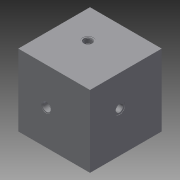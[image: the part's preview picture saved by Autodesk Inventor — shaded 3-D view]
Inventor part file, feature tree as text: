
AUTODESK INVENTOR PART (.ipt)
format: ipt  version: 2014 (Build 180170000, 170)  size: 241,152 bytes
history: native  units: mm
features: other x48, sketch x4, extrude x1
ambient origin geometry x8: Origin, YZ Plane, XZ Plane, XY Plane, X Axis, Y Axis, Z Axis, Center Point
bodies: 实体1 (feature_tree)
feature tree (53):
  extrude  "拉伸1"  TaperAngle=0.0deg  [1 undecoded]
  other  "UCS1"
  other  "UCS2"
  other  "UCS3"
  other  "UCS4"
  other  "UCS5"
  other  "UCS6"
  sketch  "草图1"  dims[d0=200.0mm d1=0.0mm]
  other  "UCS1: YZ 平面"
  other  "UCS1: XZ 平面"
  other  "UCS1: XY 平面"
  other  "UCS1: X 轴"
  other  "UCS1: Y 轴"
  other  "UCS1: Z 轴"
  other  "UCS1: 原点"
  other  "UCS2: YZ 平面"
  other  "UCS2: XZ 平面"
  other  "UCS2: XY 平面"
  other  "UCS2: X 轴"
  other  "UCS2: Y 轴"
  other  "UCS2: Z 轴"
  other  "UCS2: 原点"
  other  "UCS3: YZ 平面"
  other  "UCS3: XZ 平面"
  other  "UCS3: XY 平面"
  other  "UCS3: X 轴"
  other  "UCS3: Y 轴"
  other  "UCS3: Z 轴"
  other  "UCS3: 原点"
  other  "UCS4: YZ 平面"
  other  "UCS4: XZ 平面"
  other  "UCS4: XY 平面"
  other  "UCS4: X 轴"
  other  "UCS4: Y 轴"
  other  "UCS4: Z 轴"
  other  "UCS4: 原点"
  other  "UCS5: YZ 平面"
  other  "UCS5: XZ 平面"
  other  "UCS5: XY 平面"
  other  "UCS5: X 轴"
  other  "UCS5: Y 轴"
  other  "UCS5: Z 轴"
  other  "UCS5: 原点"
  other  "UCS6: YZ 平面"
  other  "UCS6: XZ 平面"
  other  "UCS6: XY 平面"
  other  "UCS6: X 轴"
  other  "UCS6: Y 轴"
  other  "UCS6: Z 轴"
  other  "UCS6: 原点"
  sketch  "草图2"  dims[d2=0.0mm d3=0.0mm d4=0.0mm d5=0.0mm d6=0.0mm d7=0.0mm]
  sketch  "草图3"  dims[d8=0.0mm d9=0.0mm d10=0.0mm d11=0.0mm d12=0.0mm d13=0.0mm]
  sketch  "草图4"  dims[d14=0.0mm d15=0.0mm d16=0.0mm d17=0.0mm d18=0.0mm d19=0.0mm d20=0.0mm d21=0.0mm d22=0.0mm d23=0.0mm d24=0.0mm d25=0.0mm d26=0.0mm d27=0.0mm d28=0.0mm d29=0.0mm d30=0.0mm d31=0.0mm d32=0.0mm d33=0.0mm d34=0.0mm d35=0.0mm d36=0.0mm d37=0.0mm d38=0.0mm d42=0.0mm d46=0.0mm d47=0.0mm]
note: 1 required parameter value undecoded (feature->parameter linkage not recoverable at this tier; creation-order binding heuristic only, values carry confidence <= 0.55)
